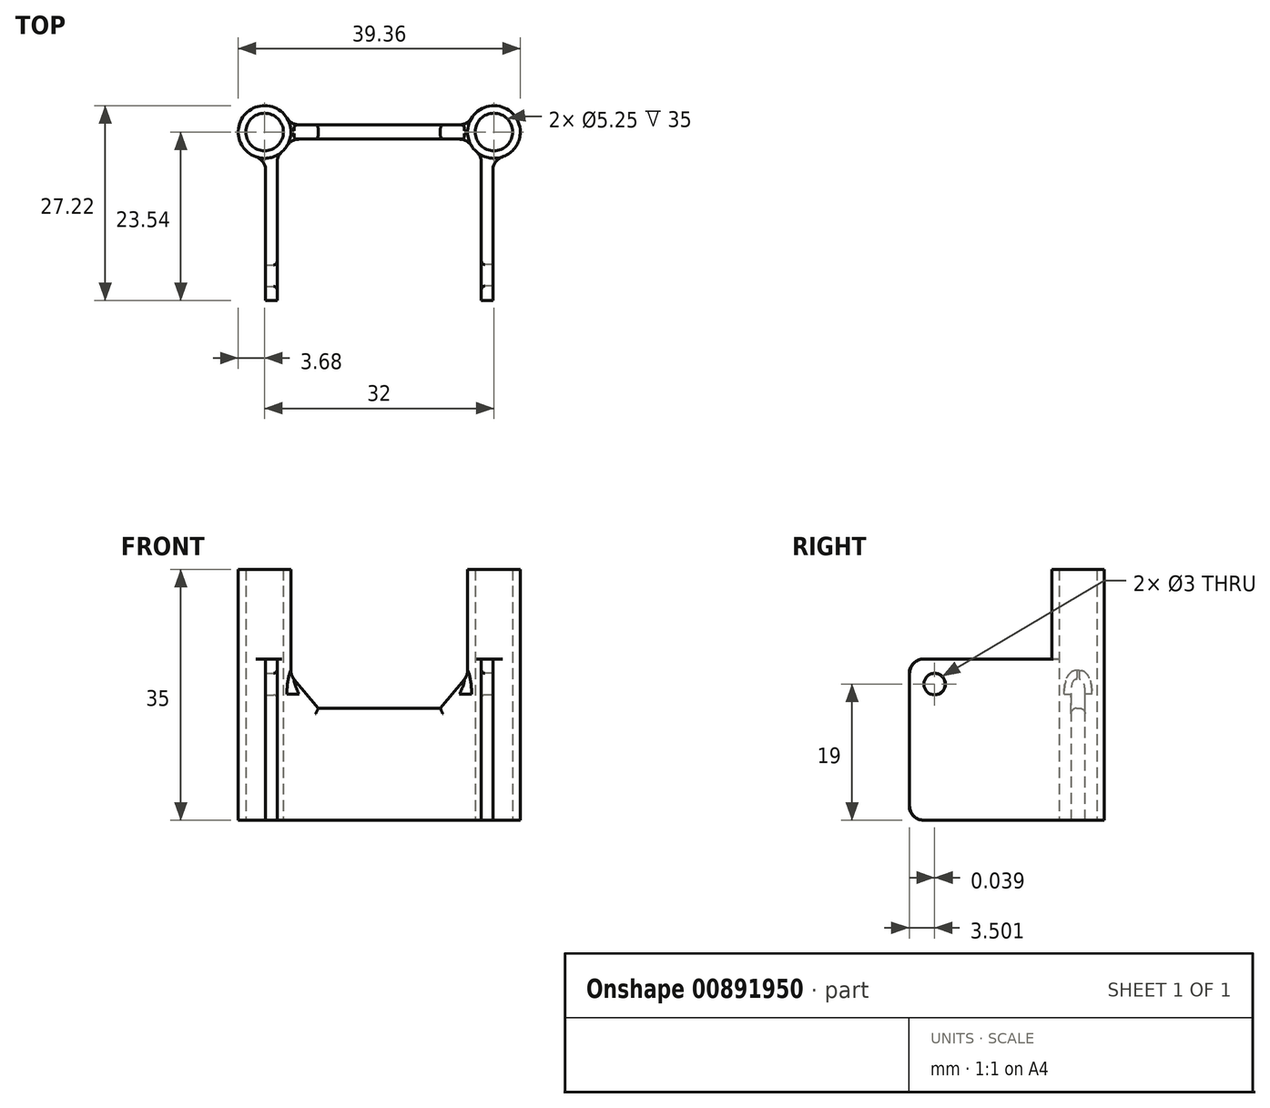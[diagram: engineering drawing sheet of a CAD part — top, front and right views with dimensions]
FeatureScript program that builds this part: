
annotation { "Feature Type Name" : "Feature", "Feature Type Description" : "" }
export const myFeature = defineFeature(function(context is Context, id is Id, definition is map)
    precondition{}
    {
        {
            var Q0;
            Q0=qCreatedBy(makeId("Top.planeOp"),FACE);
            var sketch = newSketch(context, id + "F0", { "sketchPlane" : qUnion([Q0])});
            skCircle(sketch, "E0", {"center": v(-16, 0) * mm, "radius": 3.67 * mm});
            skCircle(sketch, "E1", {"center": v(16, 0) * mm, "radius": 3.67 * mm});
            skSolve(sketch);
        }
        {
            var Q0;
            Q0=qSketchRegion(id+"F0",true);
            extrude(context, id + "F1", {"entities" : qUnion([Q0]), "offsetDistance" : 25 * mm, "depth" : 35 * mm});
        }
        {
            var Q0;
            Q0=qCreatedBy(makeId("Front.planeOp"),FACE);
            var sketch = newSketch(context, id + "F2", { "sketchPlane" : qUnion([Q0])});
            skLineSegment(sketch, "E2", {"start": v(13, 0) * mm, "end": v(13, 21) * mm});
            skLineSegment(sketch, "E3", {"start": v(13, 21) * mm, "end": v(13, 21) * mm});
            skLineSegment(sketch, "E4", {"start": v(13, 21) * mm, "end": v(8.5, 15.64) * mm});
            skLineSegment(sketch, "E5", {"start": v(8.5, 15.64) * mm, "end": v(-8.5, 15.64) * mm});
            skLineSegment(sketch, "E6", {"start": v(-8.5, 15.64) * mm, "end": v(-13, 21) * mm});
            skLineSegment(sketch, "E7", {"start": v(-13, 21) * mm, "end": v(-13, 0) * mm});
            skLineSegment(sketch, "E8", {"start": v(-13, 0) * mm, "end": v(13, 0) * mm});
            skSolve(sketch);
        }
        {
            var Q0;
            Q0=makeQuery(id+"F2.imprint","IMPRINT",FACE,{"disambiguationData":[TD([[makeQuery(id+"F2.imprint","IMPRINT",EDGE,{"derivedFrom":sQuery(id+"F2.wireOp",EDGE,"E2")}),1.0]])]});
            extrude(context, id + "F3", {"entities" : qUnion([Q0]), "depth" : 2 * mm, "symmetric" : true});
        }
        {
            var Q0;
            Q0=qCreatedBy(makeId("Right.planeOp"),FACE);
            var Q1;
            Q1=qBodyType(qCreatedBy(id+"F5",EDGE),BodyType.WIRE);
            cPlane(context, id + "F4", {"entities" : qUnion([Q0, Q1]), "cplaneType" : CPlaneType.OFFSET, "offset" : 14.25 * mm, "width" : 150 * mm, "height" : 150 * mm});
        }
        {
            var Q0;
            Q0=qCreatedBy(id+"F4.planeOp",FACE);
            var sketch = newSketch(context, id + "F5", { "sketchPlane" : qUnion([Q0])});
            skCircle(sketch, "E9", {"center": v(-20, 19) * mm, "radius": 1.5 * mm});
            skLineSegment(sketch, "E10", {"start": v(0, 0) * mm, "end": v(-21.5, 0) * mm});
            skLineSegment(sketch, "E11", {"start": v(-23.5, 2) * mm, "end": v(-23.5, 20.5) * mm});
            skLineSegment(sketch, "E12", {"start": v(-21.5, 22.5) * mm, "end": v(0, 22.5) * mm});
            skLineSegment(sketch, "E13", {"start": v(0, 22.5) * mm, "end": v(0, 0) * mm});
            skPoint(sketch, "E14.visualSharp", {"position": v(-23.5, 22.5) * mm});
            skArc(sketch, "E14.filletArc", {"start": v(-21.5, 22.5) * mm, "mid": v(-22.91, 21.91) * mm, "end": v(-23.5, 20.5) * mm});
            skPoint(sketch, "E15.visualSharp", {"position": v(-23.5, 0) * mm});
            skArc(sketch, "E15.filletArc", {"start": v(-23.5, 2) * mm, "mid": v(-22.91, 0.59) * mm, "end": v(-21.5, 0) * mm});
            skSolve(sketch);
        }
        {
            var Q0;
            Q0=qSketchRegion(id+"F5",true);
            extrude(context, id + "F6", {"entities" : qUnion([Q0]), "operationType" : NewBodyOperationType.ADD, "depth" : 1.6 * mm});
        }
        {
            var Q0;
            Q0=qCreatedBy(makeId("Right.planeOp"),FACE);
            cPlane(context, id + "F7", {"entities" : qUnion([Q0]), "cplaneType" : CPlaneType.OFFSET, "offset" : 14.25 * mm, "oppositeDirection" : true, "width" : 150 * mm, "height" : 150 * mm});
        }
        {
            var Q0;
            Q0=qCreatedBy(id+"F7.planeOp",FACE);
            var sketch = newSketch(context, id + "F8", { "sketchPlane" : qUnion([Q0])});
            skCircle(sketch, "E16", {"center": v(-20.04, 19) * mm, "radius": 1.5 * mm});
            skLineSegment(sketch, "E17", {"start": v(-0.04, 0) * mm, "end": v(-21.54, 0) * mm});
            skLineSegment(sketch, "E18", {"start": v(-23.54, 2) * mm, "end": v(-23.54, 20.5) * mm});
            skLineSegment(sketch, "E19", {"start": v(-21.54, 22.5) * mm, "end": v(-0.04, 22.5) * mm});
            skLineSegment(sketch, "E20", {"start": v(-0.04, 22.5) * mm, "end": v(-0.04, 0) * mm});
            skPoint(sketch, "E21.visualSharp", {"position": v(-23.54, 22.5) * mm});
            skArc(sketch, "E21.filletArc", {"start": v(-21.54, 22.5) * mm, "mid": v(-22.95, 21.91) * mm, "end": v(-23.54, 20.5) * mm});
            skPoint(sketch, "E22.visualSharp", {"position": v(-23.54, 0) * mm});
            skArc(sketch, "E22.filletArc", {"start": v(-23.54, 2) * mm, "mid": v(-22.95, 0.59) * mm, "end": v(-21.54, 0) * mm});
            skSolve(sketch);
        }
        {
            var Q0;
            Q0=qSketchRegion(id+"F8",true);
            extrude(context, id + "F9", {"entities" : qUnion([Q0]), "operationType" : NewBodyOperationType.ADD, "oppositeDirection" : true, "depth" : 1.6 * mm});
        }
        {
            var Q0;
            Q0=qCreatedBy(makeId("Top.planeOp"),FACE);
            var sketch = newSketch(context, id + "F10", { "sketchPlane" : qUnion([Q0])});
            skCircle(sketch, "E23", {"center": v(-16, 0) * mm, "radius": 0.5 * mm});
            skCircle(sketch, "E24", {"center": v(16, 0) * mm, "radius": 1.75 * mm});
            skSolve(sketch);
        }
        {
            var Q0;
            Q0=sQuery(id+"F10.wireOp",VERTEX,"E23.center");
            var Q1;
            Q1=sQuery(id+"F10.wireOp",VERTEX,"E24.center");
            var Q2;
            Q2=makeQuery(id+"F1.opExtrude","SWEPT_BODY",BODY,{"disambiguationData":[OSD([sQuery(id+"F0.wireOp",EDGE,"E0")])]});
            var Q3;
            Q3=makeQuery(id+"F3.opExtrude","SWEPT_BODY",BODY,{"disambiguationData":[OSD([sQuery(id+"F2.wireOp",EDGE,"in345Lub-D59E-tOme-60dj-Cq3KucnByxKd"),sQuery(id+"F2.wireOp",EDGE,"E2"),sQuery(id+"F2.wireOp",EDGE,"E4"),sQuery(id+"F2.wireOp",EDGE,"E5"),sQuery(id+"F2.wireOp",EDGE,"E6"),sQuery(id+"F2.wireOp",EDGE,"E7")])]});
            var Q4;
            Q4=makeQuery(id+"FYRTTrcSvXfLMjP_3.opExtrude","SWEPT_BODY",BODY,{"disambiguationData":[OSD([sQuery(id+"Fs8EBPNxBlUYa75_3.wireOp",EDGE,"JWLeMf17-8jiZ-tYXv-UtJK-ccR32AaEOkmf.bottom"),sQuery(id+"Fs8EBPNxBlUYa75_3.wireOp",EDGE,"JWLeMf17-8jiZ-tYXv-UtJK-ccR32AaEOkmf.top"),sQuery(id+"Fs8EBPNxBlUYa75_3.wireOp",EDGE,"JWLeMf17-8jiZ-tYXv-UtJK-ccR32AaEOkmf.left"),sQuery(id+"Fs8EBPNxBlUYa75_3.wireOp",EDGE,"JWLeMf17-8jiZ-tYXv-UtJK-ccR32AaEOkmf.right")])]});
            var Q5;
            Q5=makeQuery(id+"F1.opExtrude","SWEPT_BODY",BODY,{"disambiguationData":[OSD([sQuery(id+"F0.wireOp",EDGE,"E1")])]});
            var Q6;
            Q6=makeQuery(id+"FYRTTrcSvXfLMjP_3.opExtrude","SWEPT_BODY",BODY,{"disambiguationData":[OSD([sQuery(id+"Fs8EBPNxBlUYa75_3.wireOp",EDGE,"dHJZYZbQ-VqZX-6sAW-GdeU-ZCC2gI22Ho79.bottom"),sQuery(id+"Fs8EBPNxBlUYa75_3.wireOp",EDGE,"dHJZYZbQ-VqZX-6sAW-GdeU-ZCC2gI22Ho79.top"),sQuery(id+"Fs8EBPNxBlUYa75_3.wireOp",EDGE,"dHJZYZbQ-VqZX-6sAW-GdeU-ZCC2gI22Ho79.left"),sQuery(id+"Fs8EBPNxBlUYa75_3.wireOp",EDGE,"dHJZYZbQ-VqZX-6sAW-GdeU-ZCC2gI22Ho79.right")])]});
            hole(context, id + "F11", {"style" : HoleStyle.SIMPLE, "endStyle" : HoleEndStyle.THROUGH, "oppositeDirection" : true, "holeDiameter" : 5.25 * mm, "majorDiameter" : 5 * mm, "isTappedThrough" : true, "tappedDepth" : 12 * mm, "tapClearance" : 3, "locations" : qUnion([Q0, Q1]), "scope" : qUnion([Q2, Q3, Q4, Q5, Q6])});
        }
        {
            var Q0;
            Q0=makeQuery(id+"F1.opExtrude","SWEPT_BODY",BODY,{"disambiguationData":[OSD([sQuery(id+"F0.wireOp",EDGE,"E1")])]});
            var Q1;
            Q1=makeQuery(id+"F3.opExtrude","SWEPT_BODY",BODY,{"disambiguationData":[OSD([sQuery(id+"F2.wireOp",EDGE,"in345Lub-D59E-tOme-60dj-Cq3KucnByxKd"),sQuery(id+"F2.wireOp",EDGE,"E2"),sQuery(id+"F2.wireOp",EDGE,"E4"),sQuery(id+"F2.wireOp",EDGE,"E5"),sQuery(id+"F2.wireOp",EDGE,"E6"),sQuery(id+"F2.wireOp",EDGE,"E7")])]});
            var Q2;
            Q2=makeQuery(id+"F1.opExtrude","SWEPT_BODY",BODY,{"disambiguationData":[OSD([sQuery(id+"F0.wireOp",EDGE,"E0")])]});
            booleanBodies(context, id + "F12", {"operationType" : BooleanOperationType.UNION, "tools" : qUnion([Q0, Q1, Q2])});
        }
        {
            var Q0;
            Q0=makeQuery(id+"F3.opExtrude","CAP_EDGE",EDGE,{"disambiguationData":[OSD([sQuery(id+"F2.wireOp",EDGE,"E5")])],"isStart":false});
            var Q1;
            Q1=makeQuery(id+"F3.opExtrude","CAP_EDGE",EDGE,{"disambiguationData":[OSD([sQuery(id+"F2.wireOp",EDGE,"E5")])],"isStart":true});
            var Q2;
            Q2=makeQuery(id+"F3.opExtrude","CAP_EDGE",EDGE,{"disambiguationData":[OSD([sQuery(id+"F2.wireOp",EDGE,"E6")])],"isStart":false});
            var Q3;
            Q3=makeQuery(id+"F3.opExtrude","CAP_EDGE",EDGE,{"disambiguationData":[OSD([sQuery(id+"F2.wireOp",EDGE,"E6")])],"isStart":true});
            var Q4;
            Q4=makeQuery(id+"F3.opExtrude","CAP_EDGE",EDGE,{"disambiguationData":[OSD([sQuery(id+"F2.wireOp",EDGE,"E4")])],"isStart":false});
            var Q5;
            Q5=makeQuery(id+"F3.opExtrude","CAP_EDGE",EDGE,{"disambiguationData":[OSD([sQuery(id+"F2.wireOp",EDGE,"E4")])],"isStart":true});
            fillet(context, id + "F13", {"entities" : qUnion([Q0, Q1, Q2, Q3, Q4, Q5]), "radius" : .8 * mm, "tangentPropagation" : true, "allowEdgeOverflow" : false});
        }
        {
            var Q0;
            Q0=makeQuery(id+"F11.hole-0.boolean.opBoolean","INTERSECT",EDGE,{"derivedFrom":[makeQuery(id+"F1.opExtrude","CAP_FACE",FACE,{"disambiguationData":[OSD([sQuery(id+"F0.wireOp",EDGE,"E0")])],"isStart":false}),makeQuery(id+"F11.hole-0.opRevolve","SWEPT_FACE",FACE,{"disambiguationData":[OSD([sQuery(id+"F11.hole-0.sketch.wireOp",EDGE,"core_line_2")])]})]});
            var Q1;
            Q1=makeQuery(id+"F11.hole-1.boolean.opBoolean","INTERSECT",EDGE,{"derivedFrom":[makeQuery(id+"F1.opExtrude","CAP_FACE",FACE,{"disambiguationData":[OSD([sQuery(id+"F0.wireOp",EDGE,"E1")])],"isStart":false}),makeQuery(id+"F11.hole-1.opRevolve","SWEPT_FACE",FACE,{"disambiguationData":[OSD([sQuery(id+"F11.hole-1.sketch.wireOp",EDGE,"core_line_2")])]})]});
            var Q2;
            Q2=makeQuery(id+"F9.opExtrude","CAP_EDGE",EDGE,{"disambiguationData":[OSD([sQuery(id+"F8.wireOp",EDGE,"E16")])],"isStart":true});
            var Q3;
            Q3=makeQuery(id+"F6.opExtrude","CAP_EDGE",EDGE,{"disambiguationData":[OSD([sQuery(id+"F5.wireOp",EDGE,"E9")])],"isStart":true});
            fillet(context, id + "F14", {"entities" : qUnion([Q0, Q1, Q2, Q3]), "radius" : .5 * mm, "tangentPropagation" : true, "allowEdgeOverflow" : false});
        }
        {
            var Q0;
            Q0=makeQuery(id+"F6.boolean.opBoolean","INTERSECT",EDGE,{"derivedFrom":[makeQuery(id+"F1.opExtrude","SWEPT_FACE",FACE,{"disambiguationData":[OSD([sQuery(id+"F0.wireOp",EDGE,"E1")])]}),makeQuery(id+"F6.opExtrude","CAP_FACE",FACE,{"disambiguationData":[OSD([sQuery(id+"F5.wireOp",EDGE,"E9"),sQuery(id+"F5.wireOp",EDGE,"E10"),sQuery(id+"F5.wireOp",EDGE,"E11"),sQuery(id+"F5.wireOp",EDGE,"E12"),sQuery(id+"F5.wireOp",EDGE,"E13"),sQuery(id+"F5.wireOp",EDGE,"E14.filletArc"),sQuery(id+"F5.wireOp",EDGE,"E15.filletArc")])],"isStart":true})]});
            var Q1;
            Q1=makeQuery(id+"F6.boolean.opBoolean","INTERSECT",EDGE,{"derivedFrom":[makeQuery(id+"F1.opExtrude","SWEPT_FACE",FACE,{"disambiguationData":[OSD([sQuery(id+"F0.wireOp",EDGE,"E1")])]}),makeQuery(id+"F6.opExtrude","CAP_FACE",FACE,{"disambiguationData":[OSD([sQuery(id+"F5.wireOp",EDGE,"E9"),sQuery(id+"F5.wireOp",EDGE,"E10"),sQuery(id+"F5.wireOp",EDGE,"E11"),sQuery(id+"F5.wireOp",EDGE,"E12"),sQuery(id+"F5.wireOp",EDGE,"E13"),sQuery(id+"F5.wireOp",EDGE,"E14.filletArc"),sQuery(id+"F5.wireOp",EDGE,"E15.filletArc")])],"isStart":false})]});
            var Q2;
            Q2=makeQuery(id+"F12.opBoolean","INTERSECT",EDGE,{"derivedFrom":[makeQuery(id+"F1.opExtrude","SWEPT_FACE",FACE,{"disambiguationData":[OSD([sQuery(id+"F0.wireOp",EDGE,"E1")])]}),makeQuery(id+"F3.opExtrude","CAP_FACE",FACE,{"disambiguationData":[OSD([sQuery(id+"F2.wireOp",EDGE,"E2"),sQuery(id+"F2.wireOp",EDGE,"E4"),sQuery(id+"F2.wireOp",EDGE,"E5"),sQuery(id+"F2.wireOp",EDGE,"E6"),sQuery(id+"F2.wireOp",EDGE,"E7"),sQuery(id+"F2.wireOp",EDGE,"E8")])],"isStart":false})]});
            var Q3;
            Q3=makeQuery(id+"F12.opBoolean","INTERSECT",EDGE,{"derivedFrom":[makeQuery(id+"F1.opExtrude","SWEPT_FACE",FACE,{"disambiguationData":[OSD([sQuery(id+"F0.wireOp",EDGE,"E0")])]}),makeQuery(id+"F3.opExtrude","CAP_FACE",FACE,{"disambiguationData":[OSD([sQuery(id+"F2.wireOp",EDGE,"E2"),sQuery(id+"F2.wireOp",EDGE,"E4"),sQuery(id+"F2.wireOp",EDGE,"E5"),sQuery(id+"F2.wireOp",EDGE,"E6"),sQuery(id+"F2.wireOp",EDGE,"E7"),sQuery(id+"F2.wireOp",EDGE,"E8")])],"isStart":false})]});
            var Q4;
            Q4=makeQuery(id+"F9.boolean.opBoolean","INTERSECT",EDGE,{"derivedFrom":[makeQuery(id+"F1.opExtrude","SWEPT_FACE",FACE,{"disambiguationData":[OSD([sQuery(id+"F0.wireOp",EDGE,"E0")])]}),makeQuery(id+"F9.opExtrude","CAP_FACE",FACE,{"disambiguationData":[OSD([sQuery(id+"F8.wireOp",EDGE,"E16"),sQuery(id+"F8.wireOp",EDGE,"E17"),sQuery(id+"F8.wireOp",EDGE,"E18"),sQuery(id+"F8.wireOp",EDGE,"E19"),sQuery(id+"F8.wireOp",EDGE,"E20"),sQuery(id+"F8.wireOp",EDGE,"E21.filletArc"),sQuery(id+"F8.wireOp",EDGE,"E22.filletArc")])],"isStart":false})]});
            var Q5;
            Q5=makeQuery(id+"F9.boolean.opBoolean","INTERSECT",EDGE,{"derivedFrom":[makeQuery(id+"F1.opExtrude","SWEPT_FACE",FACE,{"disambiguationData":[OSD([sQuery(id+"F0.wireOp",EDGE,"E0")])]}),makeQuery(id+"F9.opExtrude","CAP_FACE",FACE,{"disambiguationData":[OSD([sQuery(id+"F8.wireOp",EDGE,"E16"),sQuery(id+"F8.wireOp",EDGE,"E17"),sQuery(id+"F8.wireOp",EDGE,"E18"),sQuery(id+"F8.wireOp",EDGE,"E19"),sQuery(id+"F8.wireOp",EDGE,"E20"),sQuery(id+"F8.wireOp",EDGE,"E21.filletArc"),sQuery(id+"F8.wireOp",EDGE,"E22.filletArc")])],"isStart":true})]});
            fillet(context, id + "F15", {"entities" : qUnion([Q0, Q1, Q2, Q3, Q4, Q5]), "radius" : 2 * mm, "tangentPropagation" : true, "allowEdgeOverflow" : false});
        }
    });
